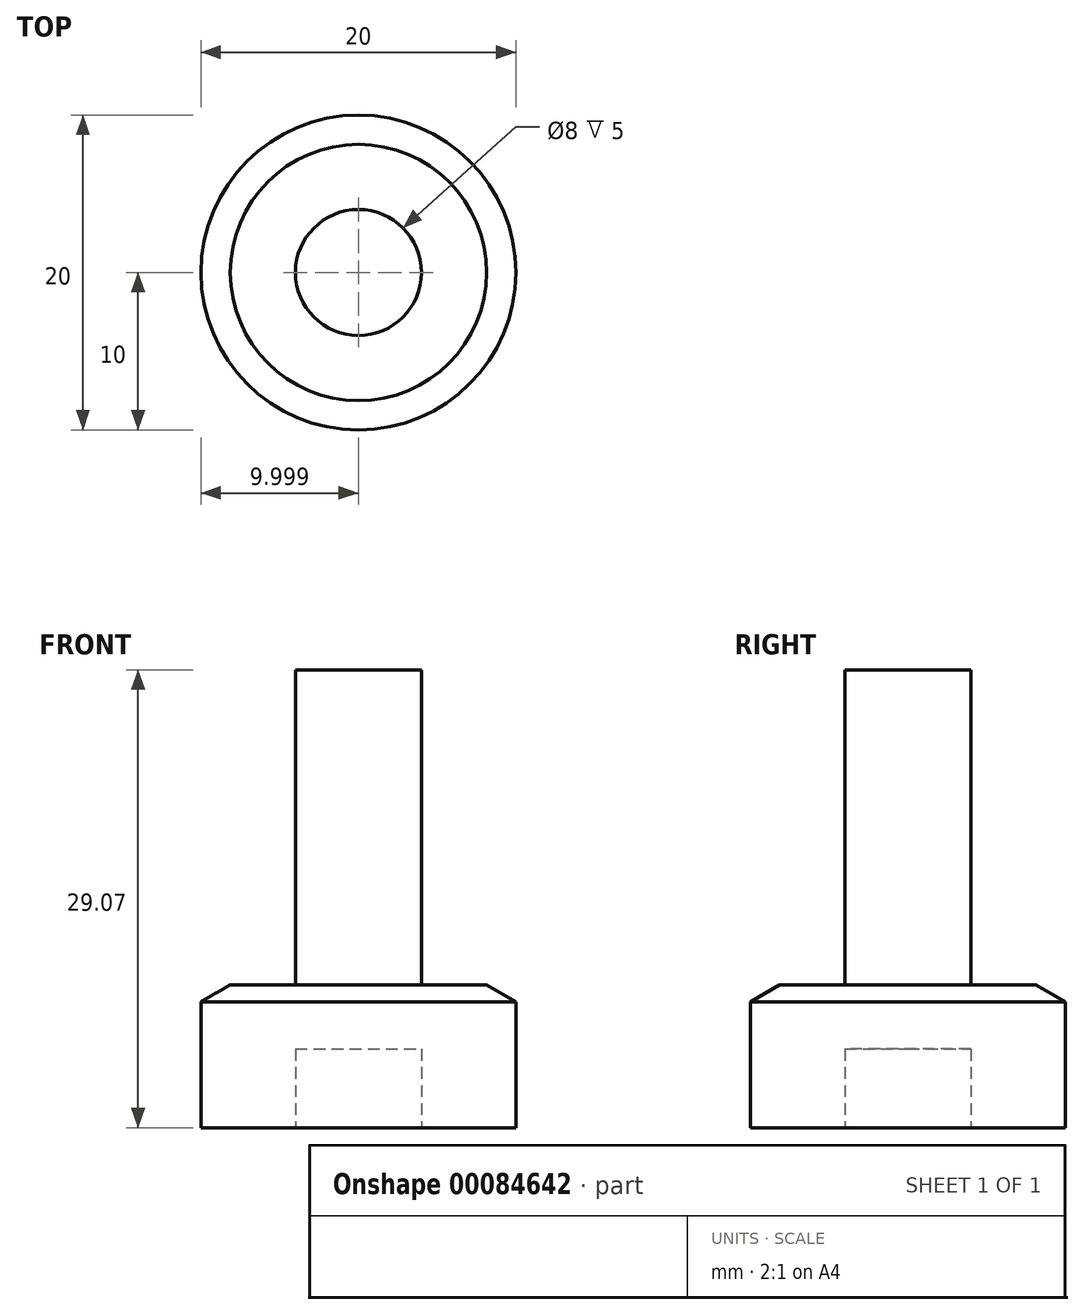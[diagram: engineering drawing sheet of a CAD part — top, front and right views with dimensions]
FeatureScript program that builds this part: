
annotation { "Feature Type Name" : "Feature", "Feature Type Description" : "" }
export const myFeature = defineFeature(function(context is Context, id is Id, definition is map)
    precondition{}
    {
        {
            var Q0;
            Q0=qCreatedBy(makeId("Front.planeOp"),FACE);
            var sketch = newSketch(context, id + "F0", { "sketchPlane" : qUnion([Q0])});
            skLineSegment(sketch, "E0.bottom", {"start": v(-30.55, 8) * mm, "end": v(-20.55, 8) * mm});
            skLineSegment(sketch, "E0.top", {"start": v(-30.55, 0) * mm, "end": v(-24.55, 0) * mm});
            skLineSegment(sketch, "E0.left", {"start": v(-30.55, 8) * mm, "end": v(-30.55, 0) * mm});
            skPoint(sketch, "E1", {"position": v(-20.55, 8) * mm});
            skPoint(sketch, "E2", {"position": v(-20.55, 0) * mm});
            skPoint(sketch, "E3", {"position": v(-20.55, 9.07) * mm});
            skLineSegment(sketch, "E4", {"start": v(-20.55, 8) * mm, "end": v(-20.55, 9.07) * mm});
            skLineSegment(sketch, "E5", {"start": v(-30.55, 8) * mm, "end": v(-28.7, 9.07) * mm});
            skLineSegment(sketch, "E6", {"start": v(-28.7, 9.07) * mm, "end": v(-20.55, 9.07) * mm});
            skLineSegment(sketch, "E7", {"start": v(-20.55, 8) * mm, "end": v(-20.55, 5) * mm});
            skPoint(sketch, "E0.right.end.orphan", {"position": v(-10.55, 0) * mm});
            skPoint(sketch, "E8.start.orphan", {"position": v(-10.55, 8) * mm});
            skLineSegment(sketch, "E9", {"start": v(-20.55, 9.07) * mm, "end": v(-20.55, 29.07) * mm});
            skLineSegment(sketch, "E10", {"start": v(-20.55, 29.07) * mm, "end": v(-24.55, 29.07) * mm});
            skLineSegment(sketch, "E11", {"start": v(-24.55, 29.07) * mm, "end": v(-24.55, 0) * mm});
            skPoint(sketch, "E12.start.orphan", {"position": v(-20.55, 4) * mm});
            skLineSegment(sketch, "E13", {"start": v(-20.55, 5) * mm, "end": v(-24.55, 5) * mm});
            skPoint(sketch, "E14", {"position": v(-20.55, 5) * mm});
            skSolve(sketch);
        }
        {
            var Q0;
            {var subQ0=sQuery(id+"F0.wireOp",EDGE,"E9");Q0=makeQuery(id+"F0.imprint","IMPRINT",FACE,{"disambiguationData":[TD([[makeQuery(id+"F0.imprint","IMPRINT",EDGE,{"derivedFrom":subQ0}),1.0]])]});}
            var Q1;
            {var subQ5=sQuery(id+"F0.wireOp",EDGE,"E0.top");Q1=makeQuery(id+"F0.imprint","IMPRINT",FACE,{"disambiguationData":[TD([[makeQuery(id+"F0.imprint","IMPRINT",EDGE,{"derivedFrom":subQ5}),1.0]])]});}
            var Q2;
            {var subQ0=sQuery(id+"F0.wireOp",EDGE,"E5");Q2=makeQuery(id+"F0.imprint","IMPRINT",FACE,{"disambiguationData":[TD([[makeQuery(id+"F0.imprint","IMPRINT",EDGE,{"derivedFrom":subQ0}),-1.0]])]});}
            var Q3;
            {var subQ0=sQuery(id+"F0.wireOp",EDGE,"E7");Q3=makeQuery(id+"F0.imprint","IMPRINT",FACE,{"disambiguationData":[TD([[makeQuery(id+"F0.imprint","IMPRINT",EDGE,{"derivedFrom":subQ0}),-1.0]])]});}
            var Q4;
            {var subQ0=sQuery(id+"F0.wireOp",EDGE,"E4");Q4=makeQuery(id+"F0.imprint","IMPRINT",FACE,{"disambiguationData":[TD([[makeQuery(id+"F0.imprint","IMPRINT",EDGE,{"derivedFrom":subQ0}),1.0]])]});}
            var Q5;
            Q5=sQuery(id+"F0.wireOp",EDGE,"E9");
            revolve(context, id + "F1", {"entities" : qUnion([Q0, Q1, Q2, Q3, Q4]), "axis" : qUnion([Q5]), "revolveType" : RevolveType.FULL});
        }
    });
